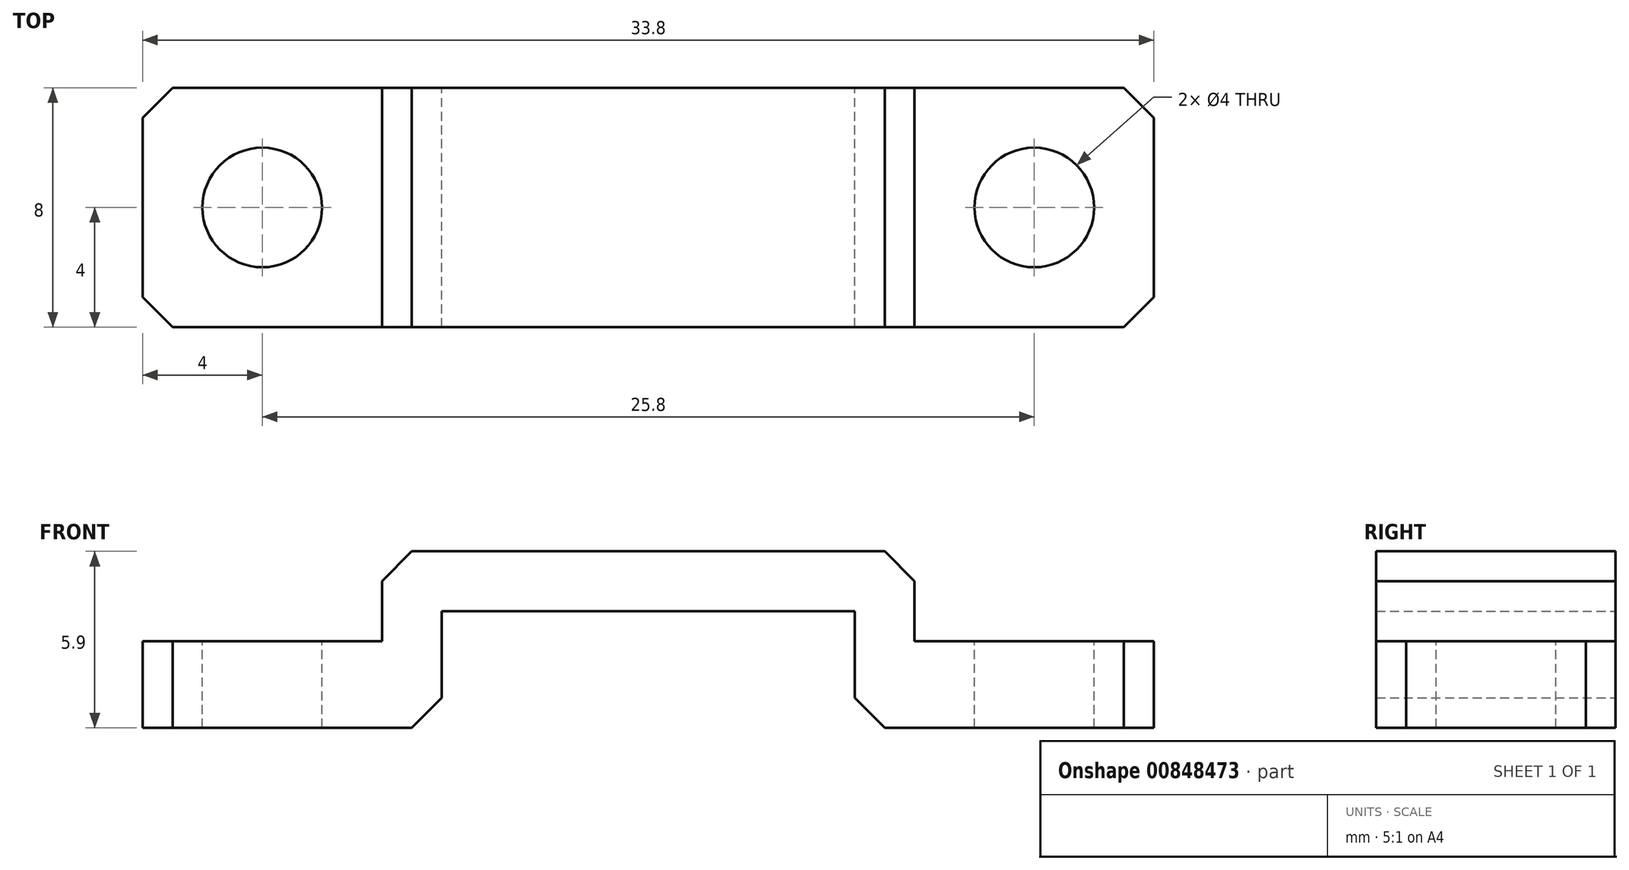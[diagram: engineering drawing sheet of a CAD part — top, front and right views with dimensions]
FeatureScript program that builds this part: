
annotation { "Feature Type Name" : "Feature", "Feature Type Description" : "" }
export const myFeature = defineFeature(function(context is Context, id is Id, definition is map)
    precondition{}
    {
        {
            var Q0;
            Q0=qCreatedBy(makeId("Top.planeOp"),FACE);
            var sketch = newSketch(context, id + "F0", { "sketchPlane" : qUnion([Q0])});
            skLineSegment(sketch, "E0.bottom", {"start": v(-6.9, -4) * mm, "end": v(6.9, -4) * mm});
            skLineSegment(sketch, "E0.top", {"start": v(-6.9, 4) * mm, "end": v(6.9, 4) * mm});
            skLineSegment(sketch, "E0.left", {"start": v(-6.9, -4) * mm, "end": v(-6.9, 4) * mm});
            skLineSegment(sketch, "E0.right", {"start": v(6.9, -4) * mm, "end": v(6.9, 4) * mm});
            skPoint(sketch, "E0.middle", {"position": v(0, 0) * mm});
            skLineSegment(sketch, "E1.0", {"start": v(-8.9, -4) * mm, "end": v(-8.9, 4) * mm});
            skLineSegment(sketch, "E2", {"start": v(-8.9, 0) * mm, "end": v(-10.9, 0) * mm, "construction": true});
            skLineSegment(sketch, "E3", {"start": v(-10.9, 0) * mm, "end": v(-12.9, 0) * mm, "construction": true});
            skLineSegment(sketch, "E4", {"start": v(-6.9, 4) * mm, "end": v(-8.9, 4) * mm});
            skLineSegment(sketch, "E5", {"start": v(-6.9, -4) * mm, "end": v(-8.9, -4) * mm});
            skCircle(sketch, "E6", {"center": v(-12.9, 0) * mm, "radius": 2 * mm});
            skLineSegment(sketch, "E7", {"start": v(-14.9, 0) * mm, "end": v(-16.9, 0) * mm, "construction": true});
            skLineSegment(sketch, "E8", {"start": v(-16.9, 0) * mm, "end": v(-16.9, -4) * mm});
            skLineSegment(sketch, "E9", {"start": v(-16.9, -4) * mm, "end": v(-8.9, -4) * mm});
            skLineSegment(sketch, "E10", {"start": v(-8.9, 4) * mm, "end": v(-16.9, 4) * mm});
            skLineSegment(sketch, "E11", {"start": v(-16.9, 4) * mm, "end": v(-16.9, 0) * mm});
            skLineSegment(sketch, "E12", {"start": v(0, 4) * mm, "end": v(0, -4) * mm, "construction": true});
            skLineSegment(sketch, "E13.MirrorCS", {"start": v(8.9, -4) * mm, "end": v(8.9, 4) * mm});
            skLineSegment(sketch, "E14.MirrorCS", {"start": v(6.9, 4) * mm, "end": v(8.9, 4) * mm});
            skLineSegment(sketch, "E15.MirrorCS", {"start": v(6.9, -4) * mm, "end": v(8.9, -4) * mm});
            skLineSegment(sketch, "E16.MirrorCS", {"start": v(16.9, -4) * mm, "end": v(8.9, -4) * mm});
            skCircle(sketch, "E17.MirrorC", {"center": v(12.9, 0) * mm, "radius": 2 * mm});
            skLineSegment(sketch, "E18.MirrorCS", {"start": v(16.9, 0) * mm, "end": v(16.9, -4) * mm});
            skLineSegment(sketch, "E19.MirrorCS", {"start": v(16.9, 4) * mm, "end": v(16.9, 0) * mm});
            skLineSegment(sketch, "E20.MirrorCS", {"start": v(8.9, 4) * mm, "end": v(16.9, 4) * mm});
            skSolve(sketch);
        }
        {
            var Q0;
            Q0=makeQuery(id+"F0.imprint","IMPRINT",FACE,{"disambiguationData":[TD([[makeQuery(id+"F0.imprint","IMPRINT",EDGE,{"derivedFrom":sQuery(id+"F0.wireOp",EDGE,"E0.left")}),1.0]])]});
            var Q1;
            Q1=makeQuery(id+"F0.imprint","IMPRINT",FACE,{"disambiguationData":[TD([[makeQuery(id+"F0.imprint","IMPRINT",EDGE,{"derivedFrom":sQuery(id+"F0.wireOp",EDGE,"E0.bottom")}),1.0]])]});
            var Q2;
            Q2=makeQuery(id+"F0.imprint","IMPRINT",FACE,{"disambiguationData":[TD([[makeQuery(id+"F0.imprint","IMPRINT",EDGE,{"derivedFrom":sQuery(id+"F0.wireOp",EDGE,"E0.right")}),-1.0]])]});
            var Q3;
            Q3=sQuery(id+"F0.wireOp",EDGE,"E7");
            extrude(context, id + "F1", {"entities" : qUnion([Q0, Q1, Q2]), "surfaceEntities" : qUnion([Q3]), "depth" : 2 * mm, "offsetDistance" : 25 * mm});
        }
        {
            var Q0;
            Q0=makeQuery(id+"F0.imprint","IMPRINT",FACE,{"disambiguationData":[TD([[makeQuery(id+"F0.imprint","IMPRINT",EDGE,{"derivedFrom":sQuery(id+"F0.wireOp",EDGE,"E0.left")}),1.0]])]});
            var Q1;
            Q1=makeQuery(id+"F0.imprint","IMPRINT",FACE,{"disambiguationData":[TD([[makeQuery(id+"F0.imprint","IMPRINT",EDGE,{"derivedFrom":sQuery(id+"F0.wireOp",EDGE,"E1.0")}),1.0]])]});
            var Q2;
            Q2=makeQuery(id+"F0.imprint","IMPRINT",FACE,{"disambiguationData":[TD([[makeQuery(id+"F0.imprint","IMPRINT",EDGE,{"derivedFrom":sQuery(id+"F0.wireOp",EDGE,"E0.right")}),-1.0]])]});
            var Q3;
            Q3=makeQuery(id+"F0.imprint","IMPRINT",FACE,{"disambiguationData":[TD([[makeQuery(id+"F0.imprint","IMPRINT",EDGE,{"derivedFrom":sQuery(id+"F0.wireOp",EDGE,"E13.MirrorCS")}),-1.0]])]});
            extrude(context, id + "F2", {"entities" : qUnion([Q0, Q1, Q2, Q3]), "operationType" : NewBodyOperationType.ADD, "oppositeDirection" : true, "depth" : 3.9 * mm, "offsetDistance" : 25 * mm});
        }
        {
            var Q0;
            Q0=makeQuery(id+"F0.imprint","IMPRINT",FACE,{"disambiguationData":[TD([[makeQuery(id+"F0.imprint","IMPRINT",EDGE,{"derivedFrom":sQuery(id+"F0.wireOp",EDGE,"E1.0")}),1.0]])]});
            var Q1;
            Q1=makeQuery(id+"F0.imprint","IMPRINT",FACE,{"disambiguationData":[TD([[makeQuery(id+"F0.imprint","IMPRINT",EDGE,{"derivedFrom":sQuery(id+"F0.wireOp",EDGE,"E13.MirrorCS")}),-1.0]])]});
            extrude(context, id + "F3", {"entities" : qUnion([Q0, Q1]), "operationType" : NewBodyOperationType.REMOVE, "oppositeDirection" : true, "depth" : 1 * mm, "offsetDistance" : 25 * mm});
        }
        {
            var Q0;
            Q0=makeQuery(id+"F1.opExtrude","CAP_EDGE",EDGE,{"disambiguationData":[OSD([sQuery(id+"F0.wireOp",EDGE,"E1.0")])],"isStart":false});
            var Q1;
            Q1=makeQuery(id+"F1.opExtrude","CAP_EDGE",EDGE,{"disambiguationData":[OSD([sQuery(id+"F0.wireOp",EDGE,"E13.MirrorCS")])],"isStart":false});
            var Q2;
            Q2=makeQuery(id+"F2.opExtrude","CAP_EDGE",EDGE,{"disambiguationData":[OSD([sQuery(id+"F0.wireOp",EDGE,"E0.left")])],"isStart":false});
            var Q3;
            Q3=makeQuery(id+"F3.boolean.opBoolean","COPY",EDGE,{"derivedFrom":makeQuery(id+"F3.opExtrude","CAP_EDGE",EDGE,{"disambiguationData":[OSD([sQuery(id+"F0.wireOp",EDGE,"E6")])],"isStart":false})});
            var Q4;
            Q4=makeQuery(id+"F3.boolean.opBoolean","COPY",EDGE,{"derivedFrom":makeQuery(id+"F3.opExtrude","CAP_EDGE",EDGE,{"disambiguationData":[OSD([sQuery(id+"F0.wireOp",EDGE,"E17.MirrorC")])],"isStart":false})});
            var Q5;
            Q5=makeQuery(id+"F2.opExtrude","CAP_EDGE",EDGE,{"disambiguationData":[OSD([sQuery(id+"F0.wireOp",EDGE,"E0.right")])],"isStart":false});
            var Q6;
            Q6=makeQuery(id+"F2.opExtrude","SWEPT_EDGE",EDGE,{"disambiguationData":[OSD([sQuery(id+"F0.wireOp",EDGE,"E8"),sQuery(id+"F0.wireOp",EDGE,"E9")])]});
            var Q7;
            Q7=makeQuery(id+"F2.opExtrude","SWEPT_EDGE",EDGE,{"disambiguationData":[OSD([sQuery(id+"F0.wireOp",EDGE,"E10"),sQuery(id+"F0.wireOp",EDGE,"E11")])]});
            var Q8;
            Q8=makeQuery(id+"F2.opExtrude","SWEPT_EDGE",EDGE,{"disambiguationData":[OSD([sQuery(id+"F0.wireOp",EDGE,"E16.MirrorCS"),sQuery(id+"F0.wireOp",EDGE,"E18.MirrorCS")])]});
            var Q9;
            Q9=makeQuery(id+"F2.opExtrude","SWEPT_EDGE",EDGE,{"disambiguationData":[OSD([sQuery(id+"F0.wireOp",EDGE,"E19.MirrorCS"),sQuery(id+"F0.wireOp",EDGE,"E20.MirrorCS")])]});
            chamfer(context, id + "F4", {"entities" : qUnion([Q0, Q1, Q2, Q3, Q4, Q5, Q6, Q7, Q8, Q9]), "width" : 1 * mm, "tangentPropagation" : true});
        }
    });
